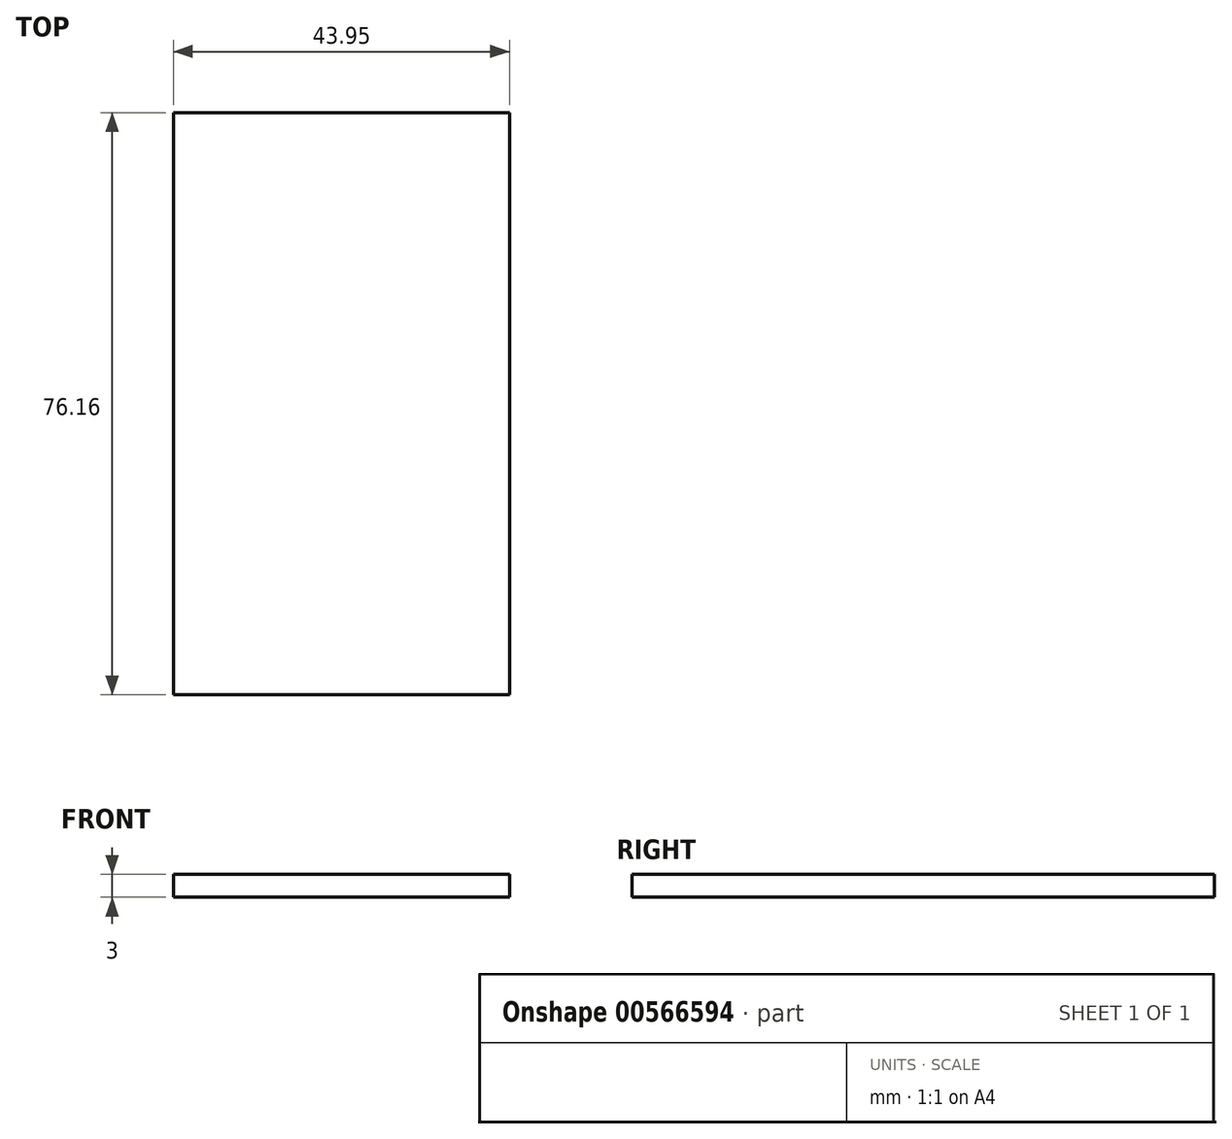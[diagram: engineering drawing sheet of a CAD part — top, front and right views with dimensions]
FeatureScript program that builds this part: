
annotation { "Feature Type Name" : "Feature", "Feature Type Description" : "" }
export const myFeature = defineFeature(function(context is Context, id is Id, definition is map)
    precondition{}
    {
        {
            var Q0;
            Q0=qCreatedBy(makeId("Top.planeOp"),FACE);
            var sketch = newSketch(context, id + "F0", { "sketchPlane" : qUnion([Q0])});
            skLineSegment(sketch, "E0.bottom", {"start": v(0, 0) * mm, "end": v(43.95, 0) * mm});
            skLineSegment(sketch, "E0.top", {"start": v(0, 76.16) * mm, "end": v(43.95, 76.16) * mm});
            skLineSegment(sketch, "E0.left", {"start": v(0, 0) * mm, "end": v(0, 76.16) * mm});
            skLineSegment(sketch, "E0.right", {"start": v(43.95, 0) * mm, "end": v(43.95, 76.16) * mm});
            skSolve(sketch);
        }
        {
            var Q0;
            Q0 = qSketchRegion(id + "F0", true);
            extrude(context, id + "F1", {"entities" : qUnion([Q0]), "depth" : 3 * mm, "offsetDistance" : 25.4 * mm});
        }
    });
